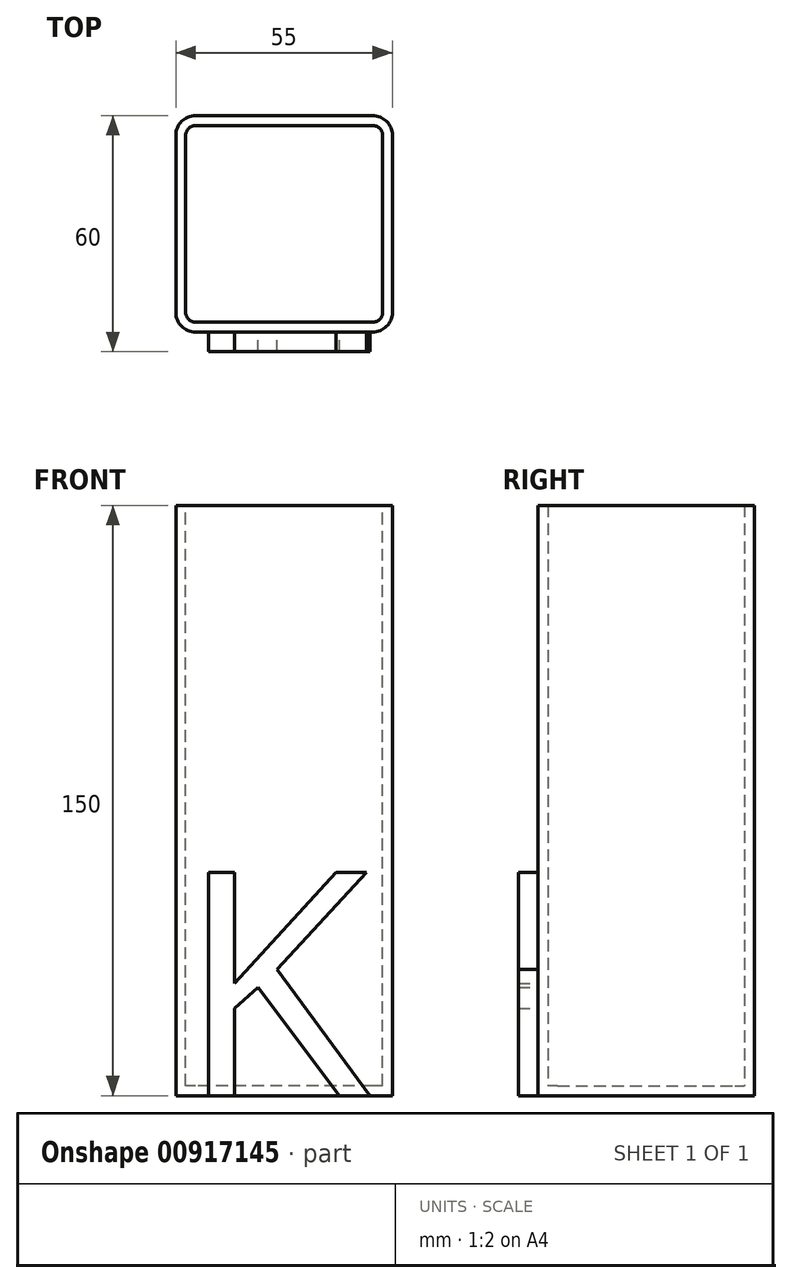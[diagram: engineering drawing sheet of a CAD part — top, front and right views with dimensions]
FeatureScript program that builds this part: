
annotation { "Feature Type Name" : "Feature", "Feature Type Description" : "" }
export const myFeature = defineFeature(function(context is Context, id is Id, definition is map)
    precondition{}
    {
        {
            var Q0;
            Q0=qCreatedBy(makeId("Top.planeOp"),FACE);
            var sketch = newSketch(context, id + "F0", { "sketchPlane" : qUnion([Q0])});
            skCircle(sketch, "E0", {"center": v(0, 0) * mm, "radius": 27.5 * mm, "construction": true});
            skLineSegment(sketch, "E1.bottom", {"start": v(22.5, -27.5) * mm, "end": v(-22.5, -27.5) * mm});
            skLineSegment(sketch, "E1.top", {"start": v(22.5, 27.5) * mm, "end": v(-22.5, 27.5) * mm});
            skLineSegment(sketch, "E1.left", {"start": v(27.5, -22.5) * mm, "end": v(27.5, 22.5) * mm});
            skLineSegment(sketch, "E1.right", {"start": v(-27.5, -22.5) * mm, "end": v(-27.5, 22.5) * mm});
            skPoint(sketch, "E2.visualSharp", {"position": v(-27.5, 27.5) * mm});
            skArc(sketch, "E2.filletArc", {"start": v(-22.5, 27.5) * mm, "mid": v(-26.04, 26.04) * mm, "end": v(-27.5, 22.5) * mm});
            skPoint(sketch, "E3.visualSharp", {"position": v(27.5, 27.5) * mm});
            skArc(sketch, "E3.filletArc", {"start": v(27.5, 22.5) * mm, "mid": v(26.04, 26.04) * mm, "end": v(22.5, 27.5) * mm});
            skPoint(sketch, "E4.visualSharp", {"position": v(27.5, -27.5) * mm});
            skArc(sketch, "E4.filletArc", {"start": v(22.5, -27.5) * mm, "mid": v(26.04, -26.04) * mm, "end": v(27.5, -22.5) * mm});
            skPoint(sketch, "E5.visualSharp", {"position": v(-27.5, -27.5) * mm});
            skArc(sketch, "E5.filletArc", {"start": v(-27.5, -22.5) * mm, "mid": v(-26.04, -26.04) * mm, "end": v(-22.5, -27.5) * mm});
            skSolve(sketch);
        }
        {
            var Q0;
            Q0 = qSketchRegion(id + "F0", true);
            extrude(context, id + "F1", {"entities" : qUnion([Q0]), "depth" : 150 * mm, "offsetDistance" : 25 * mm});
        }
        {
            var Q0;
            Q0=makeQuery(id+"F1.opExtrude","CAP_FACE",FACE,{"disambiguationData":[OSD([sQuery(id+"F0.wireOp",EDGE,"E1.bottom"),sQuery(id+"F0.wireOp",EDGE,"E1.top"),sQuery(id+"F0.wireOp",EDGE,"E1.left"),sQuery(id+"F0.wireOp",EDGE,"E1.right"),sQuery(id+"F0.wireOp",EDGE,"E2.filletArc"),sQuery(id+"F0.wireOp",EDGE,"E3.filletArc"),sQuery(id+"F0.wireOp",EDGE,"E4.filletArc"),sQuery(id+"F0.wireOp",EDGE,"E5.filletArc")])],"isStart":false});
            shell(context, id + "F2", {"entities" : qUnion([Q0]), "thickness" : 2.5 * mm});
        }
        {
            var Q0;
            Q0=makeQuery(id+"F1.opExtrude","SWEPT_FACE",FACE,{"disambiguationData":[OSD([sQuery(id+"F0.wireOp",EDGE,"E1.bottom")])]});
            var sketch = newSketch(context, id + "F3", { "sketchPlane" : qUnion([Q0])});
            skText(sketch, "E6", { "text": "K", "fontName": "OpenSans-Regular.ttf"});
            const initialGuessF3  = {"E6": [-0.02695, 0, 1, 0, 0.05719]};
            skSetInitialGuess(sketch, initialGuessF3);
            skSolve(sketch);
        }
        {
            var Q0;
            Q0 = qSketchRegion(id + "F3", true);
            extrude(context, id + "F4", {"entities" : qUnion([Q0]), "operationType" : NewBodyOperationType.ADD, "depth" : 5 * mm, "offsetDistance" : 25 * mm});
        }
    });
